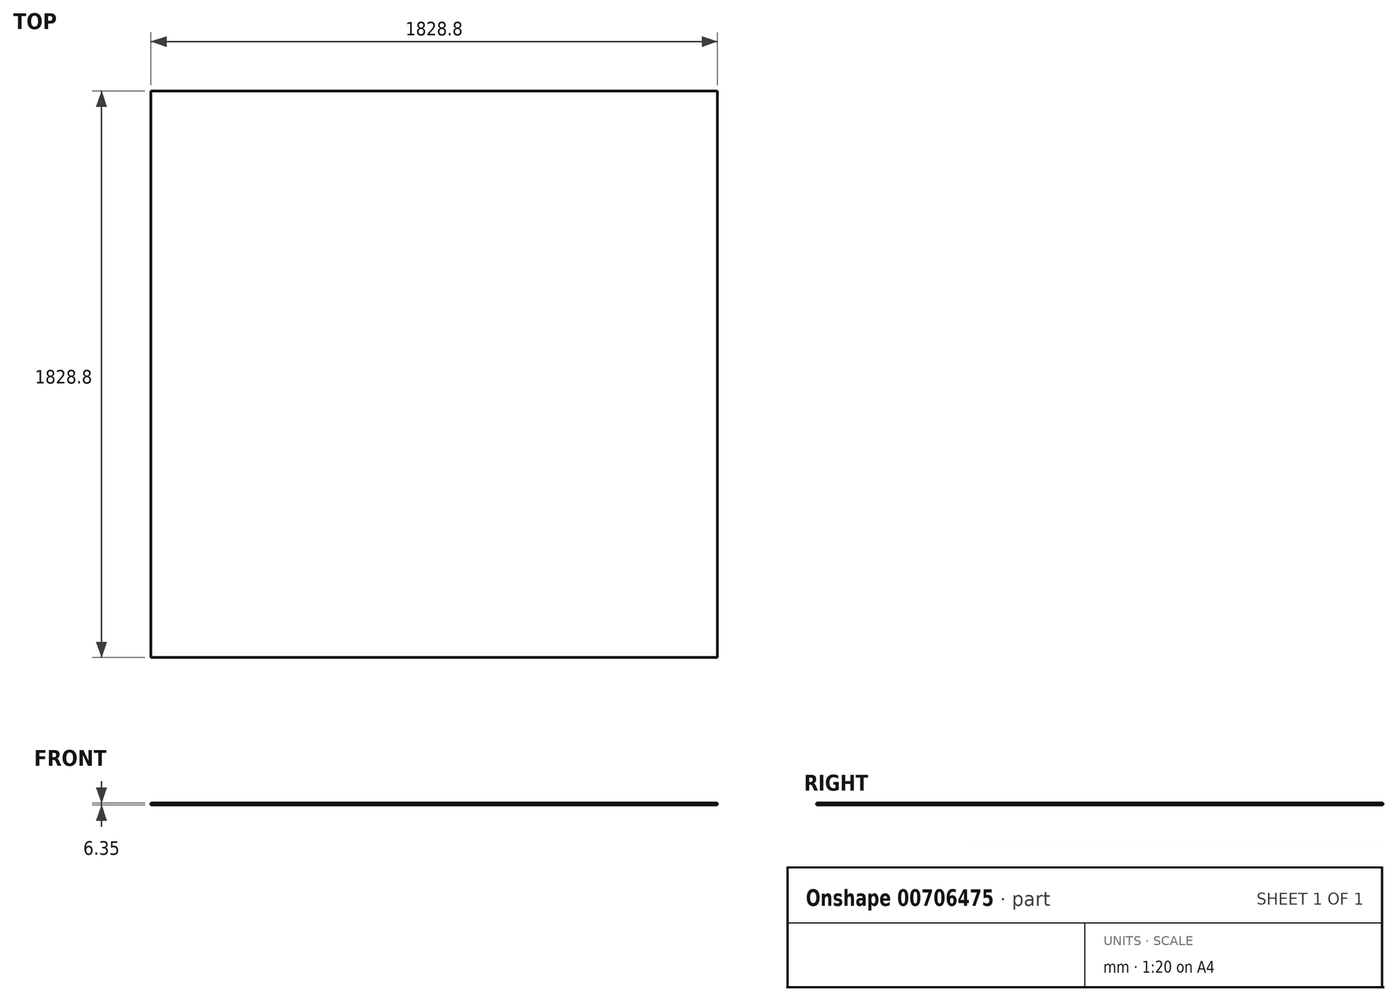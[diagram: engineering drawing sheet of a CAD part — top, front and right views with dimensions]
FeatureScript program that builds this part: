
annotation { "Feature Type Name" : "Feature", "Feature Type Description" : "" }
export const myFeature = defineFeature(function(context is Context, id is Id, definition is map)
    precondition{}
    {
        {
            var Q0;
            Q0=qCreatedBy(makeId("Top.planeOp"),FACE);
            var sketch = newSketch(context, id + "F0", { "sketchPlane" : qUnion([Q0])});
            skLineSegment(sketch, "E0.bottom", {"start": v(-910.96, 1140.63) * mm, "end": v(917.84, 1140.63) * mm});
            skLineSegment(sketch, "E0.top", {"start": v(-910.96, -688.17) * mm, "end": v(917.84, -688.17) * mm});
            skLineSegment(sketch, "E0.left", {"start": v(-910.96, 1140.63) * mm, "end": v(-910.96, -688.17) * mm});
            skLineSegment(sketch, "E0.right", {"start": v(917.84, 1140.63) * mm, "end": v(917.84, -688.17) * mm});
            skSolve(sketch);
        }
        {
            var Q0;
            Q0=makeQuery(id+"F0.imprint","IMPRINT",FACE,{"disambiguationData":[TD([[makeQuery(id+"F0.imprint","IMPRINT",EDGE,{"derivedFrom":sQuery(id+"F0.wireOp",EDGE,"E0.bottom")}),-1.0]])]});
            extrude(context, id + "F1", {"entities" : qUnion([Q0]), "depth" : 6.35 * mm, "offsetDistance" : 25.4 * mm});
        }
    });
